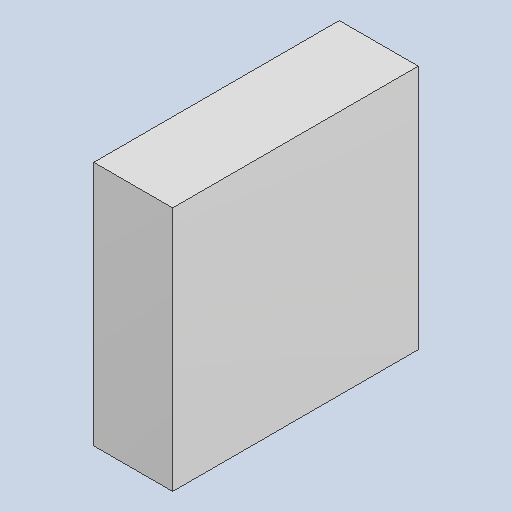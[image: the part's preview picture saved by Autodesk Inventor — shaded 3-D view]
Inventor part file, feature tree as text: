
AUTODESK INVENTOR PART (.ipt)
format: ipt  version: 2023.4 (Build 274418000, 418)  size: 81,408 bytes
history: native  units: mm
features: extrude x1
ambient origin geometry x8: Origin, YZ Plane, XZ Plane, XY Plane, X Axis, Y Axis, Z Axis, Center Point
bodies: Solid1 (feature_tree)
feature tree (1):
  extrude  "Extruded_3"  [1 undecoded]
note: 1 required parameter value undecoded (feature->parameter linkage not recoverable at this tier; creation-order binding heuristic only, values carry confidence <= 0.55)
